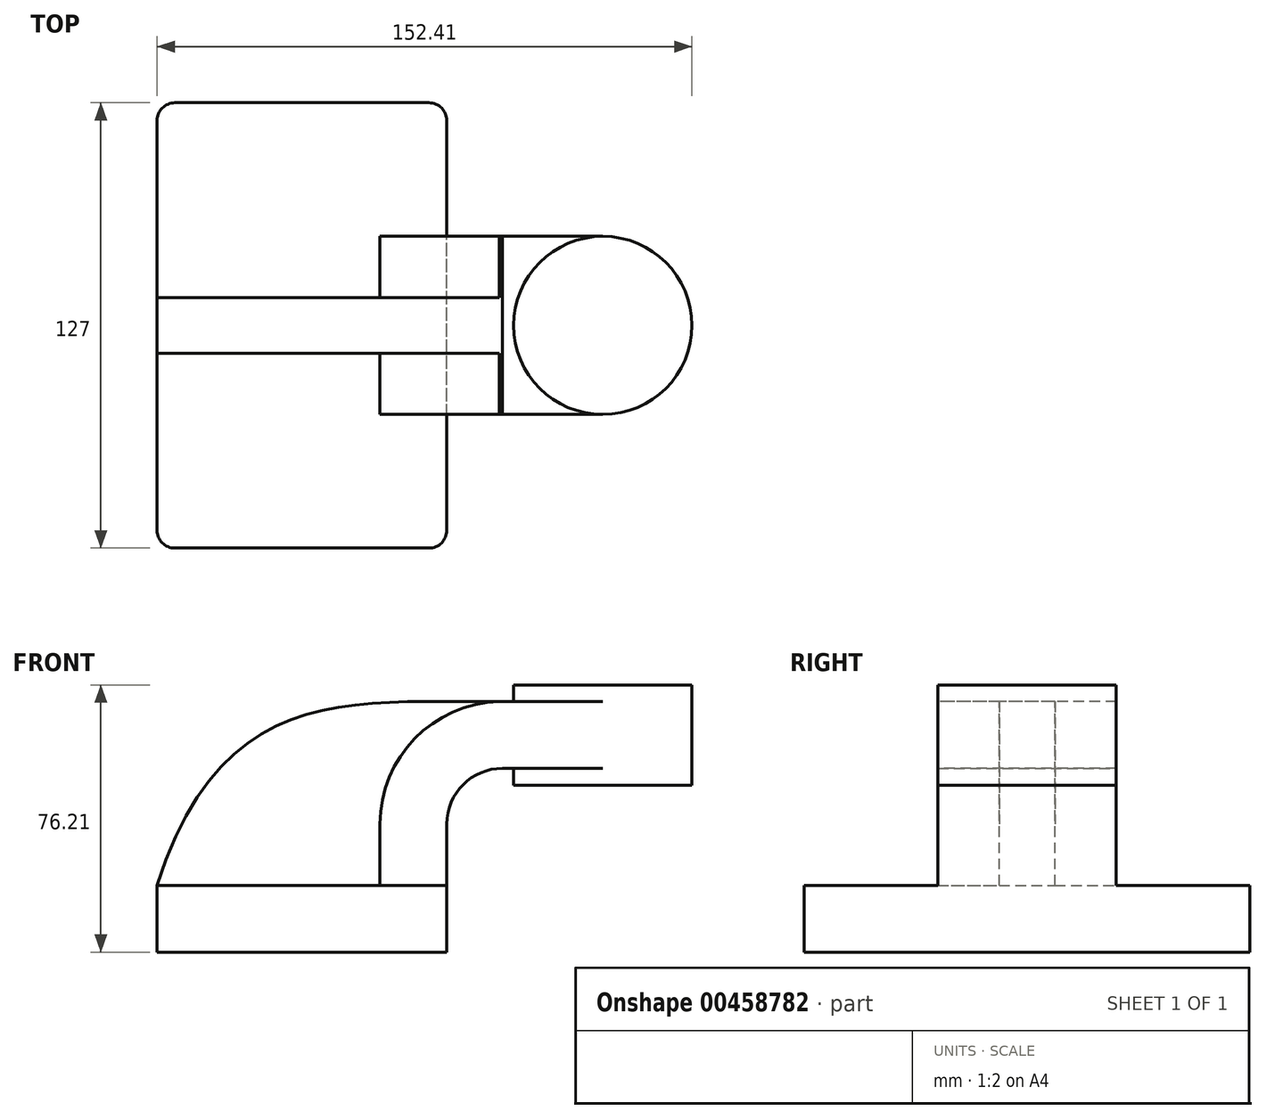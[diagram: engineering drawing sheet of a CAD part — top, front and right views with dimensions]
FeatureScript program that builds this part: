
annotation { "Feature Type Name" : "Feature", "Feature Type Description" : "" }
export const myFeature = defineFeature(function(context is Context, id is Id, definition is map)
    precondition{}
    {
        {
            var Q0;
            Q0=qCreatedBy(makeId("Front.planeOp"),FACE);
            var sketch = newSketch(context, id + "F0", { "sketchPlane" : qUnion([Q0])});
            skLineSegment(sketch, "E0.bottom", {"start": v(-41.28, 9.53) * mm, "end": v(41.28, 9.53) * mm});
            skLineSegment(sketch, "E0.top", {"start": v(-41.28, -9.53) * mm, "end": v(41.28, -9.53) * mm});
            skLineSegment(sketch, "E0.left", {"start": v(-41.28, 9.53) * mm, "end": v(-41.28, -9.53) * mm});
            skLineSegment(sketch, "E0.right", {"start": v(41.28, 9.53) * mm, "end": v(41.28, -9.53) * mm});
            skPoint(sketch, "E0.middle", {"position": v(0, 0) * mm});
            skLineSegment(sketch, "E1.bottom", {"start": v(60.33, 38.1) * mm, "end": v(111.13, 38.1) * mm});
            skLineSegment(sketch, "E1.top", {"start": v(60.33, 66.67) * mm, "end": v(111.12, 66.67) * mm});
            skLineSegment(sketch, "E1.left", {"start": v(60.33, 38.1) * mm, "end": v(60.32, 66.67) * mm});
            skLineSegment(sketch, "E1.right", {"start": v(111.13, 38.1) * mm, "end": v(111.12, 66.67) * mm});
            skPoint(sketch, "E1.middle", {"position": v(85.73, 52.39) * mm});
            skLineSegment(sketch, "E2", {"start": v(41.28, 9.53) * mm, "end": v(41.28, 27) * mm});
            skArc(sketch, "E3", {"start": v(41.28, 27) * mm, "mid": v(45.92, 38.23) * mm, "end": v(57.15, 42.88) * mm});
            skLineSegment(sketch, "E4", {"start": v(57.15, 42.88) * mm, "end": v(85.73, 42.88) * mm});
            skLineSegment(sketch, "E5.0", {"start": v(57.15, 61.93) * mm, "end": v(85.73, 61.93) * mm});
            skArc(sketch, "E5.1", {"start": v(22.23, 27) * mm, "mid": v(32.45, 51.7) * mm, "end": v(57.15, 61.93) * mm});
            skLineSegment(sketch, "E5.2", {"start": v(22.23, 9.53) * mm, "end": v(22.23, 27) * mm});
            skFitSpline(sketch, "E6", {"points": [v(-41.28, 9.53) * mm, v(57.15, 61.93) * mm], "startDerivative": vector(56.48, 177.25) * mm, "endDerivative": vector(124.54, 1.87) * mm});
            skLineSegment(sketch, "E7", {"start": v(85.72, 66.67) * mm, "end": v(85.72, 38.1) * mm});
            skSolve(sketch);
        }
        {
            var Q0;
            Q0=makeQuery(id+"F0.imprint","IMPRINT",FACE,{"disambiguationData":[TD([[makeQuery(id+"F0.imprint","IMPRINT",EDGE,{"derivedFrom":sQuery(id+"F0.wireOp",EDGE,"E0.top")}),1.0]])]});
            extrude(context, id + "F1", {"entities" : qUnion([Q0]), "depth" : 127 * mm, "symmetric" : true});
        }
        {
            var Q0;
            {var subQ3=sQuery(id+"F0.wireOp",EDGE,"E5.2");Q0=makeQuery(id+"F0.imprint","IMPRINT",FACE,{"disambiguationData":[TD([[makeQuery(id+"F0.imprint","IMPRINT",EDGE,{"derivedFrom":subQ3}),1.0]])]});}
            extrude(context, id + "F2", {"entities" : qUnion([Q0]), "operationType" : NewBodyOperationType.ADD, "depth" : 15.88 * mm, "symmetric" : true});
        }
        {
            var Q0;
            {var subQ1=sQuery(id+"F0.wireOp",EDGE,"E2");Q0=makeQuery(id+"F0.imprint","IMPRINT",FACE,{"disambiguationData":[TD([[makeQuery(id+"F0.imprint","IMPRINT",EDGE,{"derivedFrom":subQ1}),1.0]])]});}
            var Q1;
            {var subQ0=sQuery(id+"F0.wireOp",EDGE,"E4");var subQ1=sQuery(id+"F0.wireOp",EDGE,"E1.left");var subQ2=makeQuery(id+"F0.imprint","INTERSECT",VERTEX,{"derivedFrom":[subQ1,subQ0]});Q1=makeQuery(id+"F0.imprint","IMPRINT",FACE,{"disambiguationData":[TD([[makeQuery(id+"F0.imprint","IMPRINT",EDGE,{"disambiguationData":[TD([[subQ2,-1.0]])],"derivedFrom":subQ1}),-1.0]])]});}
            extrude(context, id + "F3", {"entities" : qUnion([Q0, Q1]), "operationType" : NewBodyOperationType.ADD, "depth" : 50.8 * mm, "symmetric" : true});
        }
        {
            var Q0;
            {var subQ4=sQuery(id+"F0.wireOp",EDGE,"E1.right");Q0=makeQuery(id+"F0.imprint","IMPRINT",FACE,{"disambiguationData":[TD([[makeQuery(id+"F0.imprint","IMPRINT",EDGE,{"derivedFrom":subQ4}),1.0]])]});}
            var Q1;
            Q1=sQuery(id+"F0.wireOp",EDGE,"E7");
            revolve(context, id + "F4", {"operationType" : NewBodyOperationType.ADD, "entities" : qUnion([Q0]), "axis" : qUnion([Q1]), "revolveType" : RevolveType.FULL});
        }
        {
            var Q0;
            Q0=makeQuery(id+"F1.opExtrude","CAP_EDGE",EDGE,{"disambiguationData":[OSD([sQuery(id+"F0.wireOp",EDGE,"E0.right")])],"isStart":false});
            var Q1;
            Q1=makeQuery(id+"F1.opExtrude","CAP_EDGE",EDGE,{"disambiguationData":[OSD([sQuery(id+"F0.wireOp",EDGE,"E0.left")])],"isStart":false});
            var Q2;
            Q2=makeQuery(id+"F1.opExtrude","CAP_EDGE",EDGE,{"disambiguationData":[OSD([sQuery(id+"F0.wireOp",EDGE,"E0.left")])],"isStart":true});
            var Q3;
            Q3=makeQuery(id+"F1.opExtrude","CAP_EDGE",EDGE,{"disambiguationData":[OSD([sQuery(id+"F0.wireOp",EDGE,"E0.right")])],"isStart":true});
            fillet(context, id + "F5", {"entities" : qUnion([Q0, Q1, Q2, Q3]), "radius" : 5.08 * mm, "tangentPropagation" : true, "allowEdgeOverflow" : false});
        }
    });
